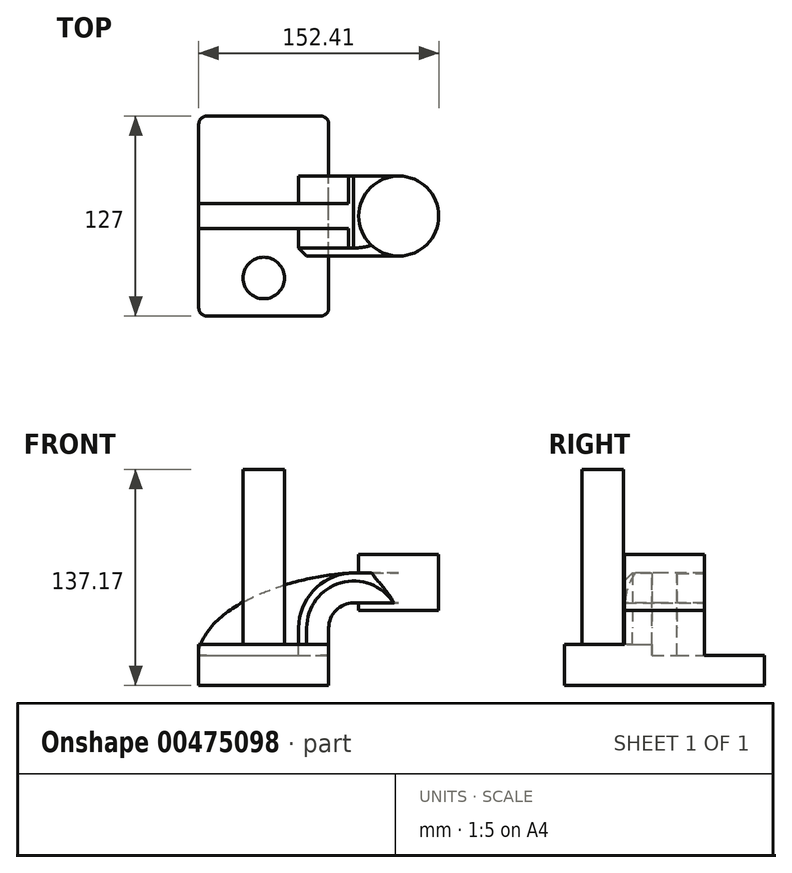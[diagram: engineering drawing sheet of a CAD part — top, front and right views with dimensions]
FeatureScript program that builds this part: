
annotation { "Feature Type Name" : "Feature", "Feature Type Description" : "" }
export const myFeature = defineFeature(function(context is Context, id is Id, definition is map)
    precondition{}
    {
        {
            var Q0;
            Q0=qCreatedBy(makeId("Front.planeOp"),FACE);
            var sketch = newSketch(context, id + "F0", { "sketchPlane" : qUnion([Q0])});
            skLineSegment(sketch, "E0.rect.bottom", {"start": v(-41.28, 9.52) * mm, "end": v(41.28, 9.52) * mm});
            skLineSegment(sketch, "E0.rect.top", {"start": v(-41.28, -9.52) * mm, "end": v(41.28, -9.52) * mm});
            skLineSegment(sketch, "E0.rect.left", {"start": v(-41.28, 9.52) * mm, "end": v(-41.28, -9.52) * mm});
            skLineSegment(sketch, "E0.rect.right", {"start": v(41.28, 9.52) * mm, "end": v(41.28, -9.52) * mm});
            skPoint(sketch, "E0.rect.middle", {"position": v(0, 0) * mm});
            skLineSegment(sketch, "E1", {"start": v(41.28, 9.52) * mm, "end": v(41.28, 27) * mm});
            skArc(sketch, "E2", {"start": v(41.28, 27) * mm, "mid": v(45.92, 38.23) * mm, "end": v(57.15, 42.88) * mm});
            skLineSegment(sketch, "E3", {"start": v(57.15, 42.88) * mm, "end": v(85.72, 42.88) * mm});
            skLineSegment(sketch, "E4.rect.bottom", {"start": v(60.32, 38.1) * mm, "end": v(111.12, 38.1) * mm});
            skLineSegment(sketch, "E4.rect.top", {"start": v(60.32, 66.68) * mm, "end": v(111.12, 66.68) * mm});
            skLineSegment(sketch, "E4.rect.left", {"start": v(60.32, 38.1) * mm, "end": v(60.32, 66.68) * mm});
            skLineSegment(sketch, "E4.rect.right", {"start": v(111.13, 38.1) * mm, "end": v(111.12, 66.68) * mm});
            skPoint(sketch, "E4.rect.middle", {"position": v(85.72, 52.39) * mm});
            skLineSegment(sketch, "E5.0", {"start": v(57.15, 61.93) * mm, "end": v(85.72, 61.93) * mm});
            skArc(sketch, "E5.1", {"start": v(22.23, 27) * mm, "mid": v(32.45, 51.7) * mm, "end": v(57.15, 61.93) * mm});
            skLineSegment(sketch, "E5.2", {"start": v(22.23, 9.52) * mm, "end": v(22.23, 27) * mm});
            skLineSegment(sketch, "E6", {"start": v(85.72, 38.1) * mm, "end": v(85.72, 66.68) * mm});
            skFitSpline(sketch, "E7", {"points": [v(-41.28, 9.53) * mm, v(57.15, 61.93) * mm], "startDerivative": vector(5.2, 92.34) * mm, "endDerivative": vector(120.92, 4.22) * mm});
            skSolve(sketch);
        }
        {
            var Q0;
            Q0=makeQuery(id+"F0.imprint","IMPRINT",FACE,{"disambiguationData":[TD([[makeQuery(id+"F0.imprint","IMPRINT",EDGE,{"derivedFrom":sQuery(id+"F0.wireOp",EDGE,"E0.rect.top")}),1.0]])]});
            extrude(context, id + "F1", {"entities" : qUnion([Q0]), "endBound" : BoundingType.SYMMETRIC, "depth" : 127 * mm});
        }
        {
            var Q0;
            {var subQ9=sQuery(id+"F0.wireOp",EDGE,"E1");Q0=makeQuery(id+"F0.imprint","IMPRINT",FACE,{"disambiguationData":[TD([[makeQuery(id+"F0.imprint","IMPRINT",EDGE,{"derivedFrom":subQ9}),1.0]])]});}
            var Q1;
            {var subQ0=sQuery(id+"F0.wireOp",EDGE,"E6");var subQ1=sQuery(id+"F0.wireOp",EDGE,"E3");var subQ2=makeQuery(id+"F0.imprint","INTERSECT",VERTEX,{"derivedFrom":[subQ1,subQ0]});Q1=makeQuery(id+"F0.imprint","IMPRINT",FACE,{"disambiguationData":[TD([[makeQuery(id+"F0.imprint","IMPRINT",EDGE,{"disambiguationData":[TD([[subQ2,1.0]])],"derivedFrom":subQ1}),1.0]])]});}
            extrude(context, id + "F2", {"entities" : qUnion([Q0, Q1]), "operationType" : NewBodyOperationType.ADD, "endBound" : BoundingType.SYMMETRIC, "depth" : 50.8 * mm});
        }
        {
            var Q0;
            {var subQ3=sQuery(id+"F0.wireOp",EDGE,"E5.2");Q0=makeQuery(id+"F0.imprint","IMPRINT",FACE,{"disambiguationData":[TD([[makeQuery(id+"F0.imprint","IMPRINT",EDGE,{"derivedFrom":subQ3}),1.0]])]});}
            extrude(context, id + "F3", {"entities" : qUnion([Q0]), "operationType" : NewBodyOperationType.ADD, "endBound" : BoundingType.SYMMETRIC, "depth" : 15.88 * mm});
        }
        {
            var Q0;
            {var subQ5=sQuery(id+"F0.wireOp",EDGE,"E4.rect.right");Q0=makeQuery(id+"F0.imprint","IMPRINT",FACE,{"disambiguationData":[TD([[makeQuery(id+"F0.imprint","IMPRINT",EDGE,{"derivedFrom":subQ5}),1.0]])]});}
            var Q1;
            Q1=sQuery(id+"F0.wireOp",EDGE,"E6");
            revolve(context, id + "F4", {"operationType" : NewBodyOperationType.ADD, "entities" : qUnion([Q0]), "axis" : qUnion([Q1]), "revolveType" : RevolveType.FULL});
        }
        {
            var Q0;
            Q0=makeQuery(id+"F1.opExtrude","CAP_EDGE",EDGE,{"disambiguationData":[OSD([sQuery(id+"F0.wireOp",EDGE,"E0.rect.right")])],"isStart":false});
            var Q1;
            Q1=makeQuery(id+"F1.opExtrude","CAP_EDGE",EDGE,{"disambiguationData":[OSD([sQuery(id+"F0.wireOp",EDGE,"E0.rect.left")])],"isStart":false});
            var Q2;
            Q2=makeQuery(id+"F1.opExtrude","CAP_EDGE",EDGE,{"disambiguationData":[OSD([sQuery(id+"F0.wireOp",EDGE,"E0.rect.right")])],"isStart":true});
            var Q3;
            Q3=makeQuery(id+"F1.opExtrude","CAP_EDGE",EDGE,{"disambiguationData":[OSD([sQuery(id+"F0.wireOp",EDGE,"E0.rect.left")])],"isStart":true});
            fillet(context, id + "F5", {"entities" : qUnion([Q0, Q1, Q2, Q3]), "radius" : 5.08 * mm, "tangentPropagation" : true, "allowEdgeOverflow" : false});
        }
        {
            var Q0;
            {var subQ4=sQuery(id+"F0.wireOp",EDGE,"E0.rect.bottom");var subQ5=sQuery(id+"F0.wireOp",EDGE,"E0.rect.right");var subQ6=sQuery(id+"F0.wireOp",EDGE,"E0.rect.left");Q0=makeQuery(id+"F3.boolean.opBoolean","SPLIT",FACE,{"disambiguationData":[TD([makeQuery(id+"F1.opExtrude","CAP_FACE",FACE,{"disambiguationData":[OSD([subQ4,sQuery(id+"F0.wireOp",EDGE,"E0.rect.top"),subQ6,subQ5])],"isStart":false})])],"derivedFrom":makeQuery(id+"F1.opExtrude","SWEPT_FACE",FACE,{"disambiguationData":[OSD([subQ4])]})});}
            var Q1;
            Q1=makeQuery(id+"F4.opRevolve","SWEPT_FACE",FACE,{"disambiguationData":[OSD([sQuery(id+"F0.wireOp",EDGE,"E4.rect.top")])]});
            extrude(context, id + "F6", {"entities" : qUnion([Q0, Q1]), "operationType" : NewBodyOperationType.ADD, "depth" : 7.11 * mm});
        }
        {
            var Q0;
            Q0=makeQuery(id+"F2.opExtrude","CAP_EDGE",EDGE,{"disambiguationData":[OSD([sQuery(id+"F0.wireOp",EDGE,"E5.1")])],"isStart":false});
            chamfer(context, id + "F7", {"entities" : qUnion([Q0]), "width" : 5.08 * mm, "tangentPropagation" : true});
        }
        {
            var Q0;
            Q0=makeQuery(id+"F6.opExtrude","CAP_FACE",FACE,{"disambiguationData":[OSD([sQuery(id+"F0.wireOp",EDGE,"E0.rect.bottom")])],"isStart":false});
            var sketch = newSketch(context, id + "F8", { "sketchPlane" : qUnion([Q0])});
            skCircle(sketch, "E8", {"center": v(0, -39.36) * mm, "radius": 13.17 * mm});
            skSolve(sketch);
        }
        {
            var Q0;
            Q0 = qSketchRegion(id + "F8", true);
            extrude(context, id + "F9", {"entities" : qUnion([Q0]), "operationType" : NewBodyOperationType.ADD, "depth" : 111 * mm});
        }
    });
